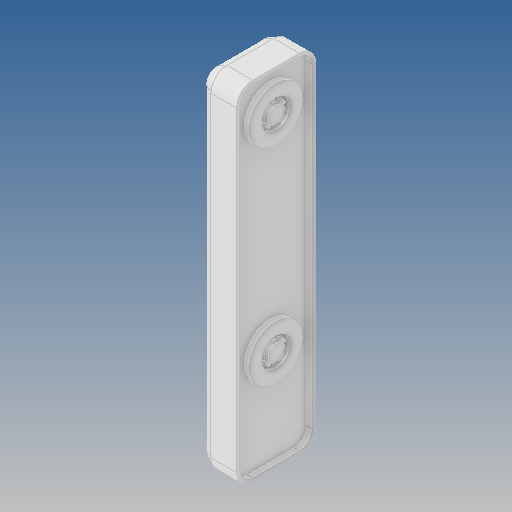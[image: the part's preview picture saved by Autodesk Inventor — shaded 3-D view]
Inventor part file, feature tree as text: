
AUTODESK INVENTOR PART (.ipt)
format: ipt  version: 2020 (Build 240168000, 168)  size: 892,416 bytes
history: native  units: mm
features: sketch x1, projected_geometry x1
ambient origin geometry x8: Origin, YZ Plane, XZ Plane, XY Plane, X Axis, Y Axis, Z Axis, Center Point
bodies: body (feature_tree), Solid1 (feature_tree)
feature tree (2):
  sketch  "Sketch1"
  projected_geometry  "Projected Loop1"
